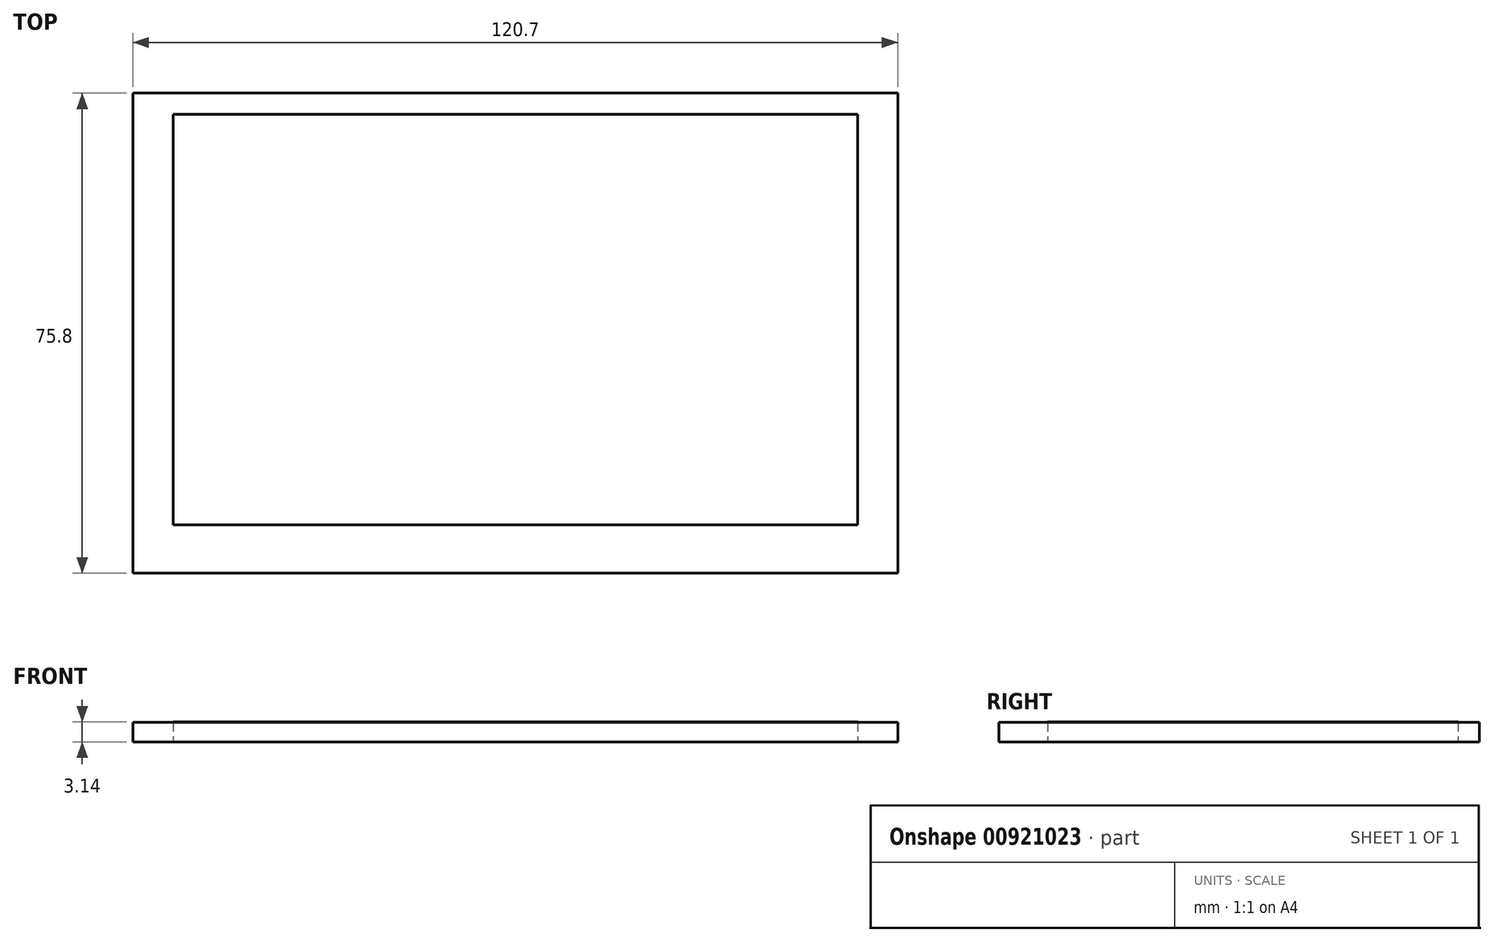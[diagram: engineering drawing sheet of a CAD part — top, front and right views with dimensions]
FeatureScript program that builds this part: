
annotation { "Feature Type Name" : "Feature", "Feature Type Description" : "" }
export const myFeature = defineFeature(function(context is Context, id is Id, definition is map)
    precondition{}
    {
        {
            var Q0;
            Q0=qCreatedBy(makeId("Top.planeOp"),FACE);
            var sketch = newSketch(context, id + "F0", { "sketchPlane" : qUnion([Q0])});
            skLineSegment(sketch, "E0.bottom", {"start": v(-60.35, 37.9) * mm, "end": v(60.35, 37.9) * mm});
            skLineSegment(sketch, "E0.top", {"start": v(-60.35, -37.9) * mm, "end": v(60.35, -37.9) * mm});
            skLineSegment(sketch, "E0.left", {"start": v(-60.35, 37.9) * mm, "end": v(-60.35, -37.9) * mm});
            skLineSegment(sketch, "E0.right", {"start": v(60.35, 37.9) * mm, "end": v(60.35, -37.9) * mm});
            skLineSegment(sketch, "E1", {"start": v(0, 37.9) * mm, "end": v(0, -37.9) * mm, "construction": true});
            skLineSegment(sketch, "E2", {"start": v(-60.35, 0) * mm, "end": v(60.35, 0) * mm, "construction": true});
            skLineSegment(sketch, "E3.bottom", {"start": v(-54, 34.53) * mm, "end": v(54, 34.53) * mm});
            skLineSegment(sketch, "E3.top", {"start": v(-54, -30.27) * mm, "end": v(54, -30.27) * mm});
            skLineSegment(sketch, "E3.left", {"start": v(-54, 34.53) * mm, "end": v(-54, -30.27) * mm});
            skLineSegment(sketch, "E3.right", {"start": v(54, 34.53) * mm, "end": v(54, -30.27) * mm});
            skPoint(sketch, "E4", {"position": v(0, 34.53) * mm});
            skSolve(sketch);
        }
        {
            var Q0;
            Q0=makeQuery(id+"F0.imprint","IMPRINT",FACE,{"disambiguationData":[TD([[makeQuery(id+"F0.imprint","IMPRINT",EDGE,{"derivedFrom":sQuery(id+"F0.wireOp",EDGE,"E0.bottom")}),-1.0]])]});
            var Q1;
            Q1=makeQuery(id+"F0.imprint","IMPRINT",FACE,{"disambiguationData":[TD([[makeQuery(id+"F0.imprint","IMPRINT",EDGE,{"derivedFrom":sQuery(id+"F0.wireOp",EDGE,"E3.bottom")}),-1.0]])]});
            extrude(context, id + "F1", {"entities" : qUnion([Q0, Q1]), "depth" : 3.1 * mm, "offsetDistance" : 25 * mm});
        }
        {
            var Q0;
            Q0=makeQuery(id+"F0.imprint","IMPRINT",FACE,{"disambiguationData":[TD([[makeQuery(id+"F0.imprint","IMPRINT",EDGE,{"derivedFrom":sQuery(id+"F0.wireOp",EDGE,"E3.bottom")}),-1.0]])]});
            extrude(context, id + "F2", {"entities" : qUnion([Q0]), "depth" : 3.14 * mm, "offsetDistance" : 25 * mm});
        }
    });
